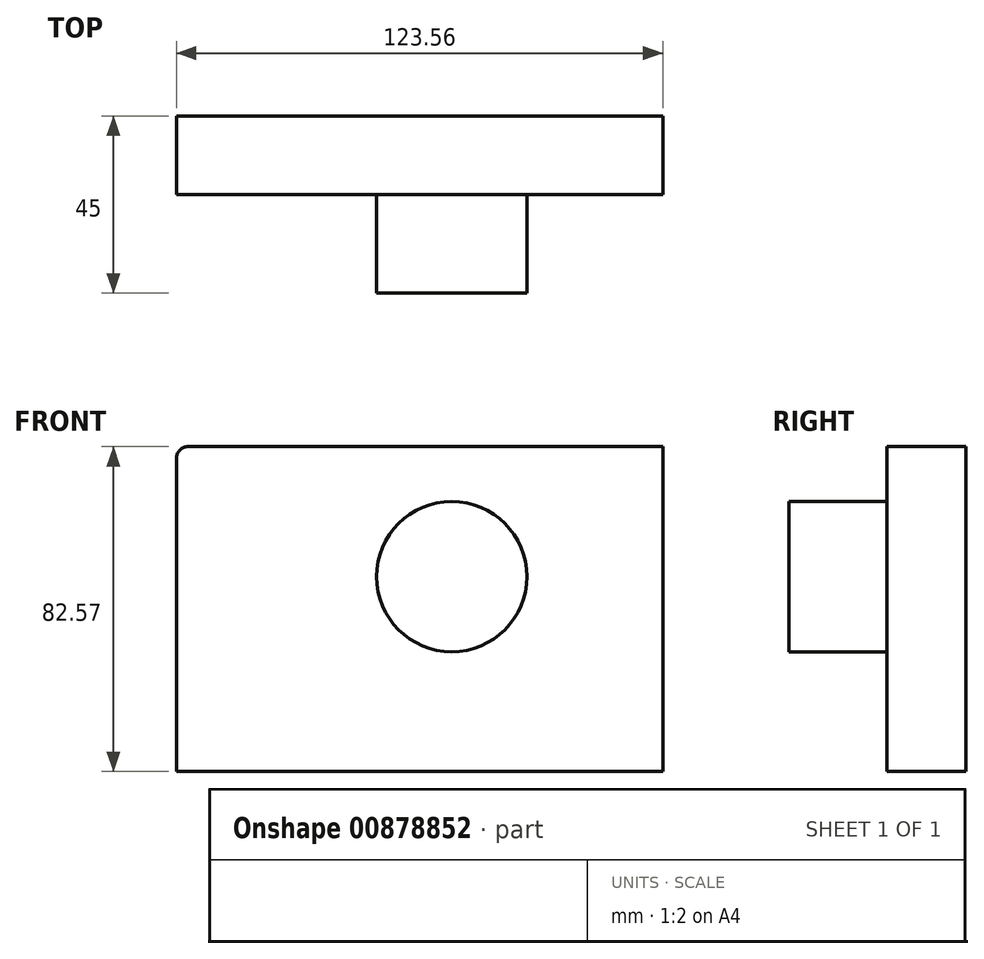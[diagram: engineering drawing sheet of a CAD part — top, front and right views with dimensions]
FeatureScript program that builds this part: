
annotation { "Feature Type Name" : "Feature", "Feature Type Description" : "" }
export const myFeature = defineFeature(function(context is Context, id is Id, definition is map)
    precondition{}
    {
        {
            var Q0;
            Q0=qCreatedBy(makeId("Front.planeOp"),FACE);
            var sketch = newSketch(context, id + "F0", { "sketchPlane" : qUnion([Q0])});
            skLineSegment(sketch, "E0.bottom", {"start": v(-66.95, 33.03) * mm, "end": v(53.6, 33.03) * mm});
            skLineSegment(sketch, "E0.top", {"start": v(-69.95, -49.54) * mm, "end": v(53.6, -49.54) * mm});
            skLineSegment(sketch, "E0.left", {"start": v(-69.95, 30.03) * mm, "end": v(-69.95, -49.54) * mm});
            skLineSegment(sketch, "E0.right", {"start": v(53.6, 33.03) * mm, "end": v(53.6, -49.54) * mm});
            skPoint(sketch, "E1.visualSharp", {"position": v(-69.95, 33.03) * mm});
            skArc(sketch, "E1.filletArc", {"start": v(-66.95, 33.03) * mm, "mid": v(-69.08, 32.15) * mm, "end": v(-69.95, 30.03) * mm});
            skSolve(sketch);
        }
        {
            var Q0;
            Q0=makeQuery(id+"F0.imprint","IMPRINT",FACE,{"disambiguationData":[TD([[makeQuery(id+"F0.imprint","IMPRINT",EDGE,{"derivedFrom":sQuery(id+"F0.wireOp",EDGE,"E0.bottom")}),-1.0]])]});
            extrude(context, id + "F1", {"entities" : qUnion([Q0]), "depth" : 20 * mm, "offsetDistance" : 25 * mm});
        }
        {
            var Q0;
            Q0=makeQuery(id+"F1.opExtrude","CAP_FACE",FACE,{"disambiguationData":[OSD([sQuery(id+"F0.wireOp",EDGE,"E0.bottom"),sQuery(id+"F0.wireOp",EDGE,"E0.top"),sQuery(id+"F0.wireOp",EDGE,"E0.left"),sQuery(id+"F0.wireOp",EDGE,"E0.right"),sQuery(id+"F0.wireOp",EDGE,"E1.filletArc")])],"isStart":false});
            var sketch = newSketch(context, id + "F2", { "sketchPlane" : qUnion([Q0])});
            skCircle(sketch, "E2", {"center": v(0, 0) * mm, "radius": 19.1 * mm});
            skSolve(sketch);
        }
        {
            var Q0;
            Q0 = qSketchRegion(id + "F2", true);
            extrude(context, id + "F3", {"entities" : qUnion([Q0]), "operationType" : NewBodyOperationType.ADD, "depth" : 25 * mm, "offsetDistance" : 25 * mm});
        }
    });
